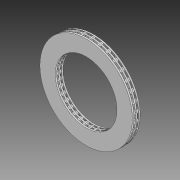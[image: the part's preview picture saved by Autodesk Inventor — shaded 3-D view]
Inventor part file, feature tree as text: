
AUTODESK INVENTOR PART (.ipt)
format: ipt  version: 2020 (Build 240168000, 168)  size: 411,136 bytes
history: native  units: mm
features: sketch x3, revolve x2, extrude x1, pattern_circular x1
ambient origin geometry x8: Origin, YZ Plane, XZ Plane, XY Plane, X Axis, Y Axis, Z Axis, Center Point
bodies: Solid1 (feature_tree)
feature tree (7):
  extrude  "Extrusion1"  Depth=60.0mm
  revolve  "Revolution1"  [1 undecoded]
  pattern_circular  "Circular Pattern1"  Count=35 Angle=360.0deg
  revolve  "Revolution2"  [1 undecoded]
  sketch  "Sketch1"  dims[d0=40.0mm d1=60.0mm]
  sketch  "Sketch2"  dims[d2=1.0mm d3=0.0mm d4=1.5mm]
  sketch  "Sketch3"  dims[d5=90.0deg d6=350.0mm d7=360.0deg d9=1.0mm d10=1.0mm d11=90.0deg]
note: 2 required parameter values undecoded (feature->parameter linkage not recoverable at this tier; creation-order binding heuristic only, values carry confidence <= 0.55)
